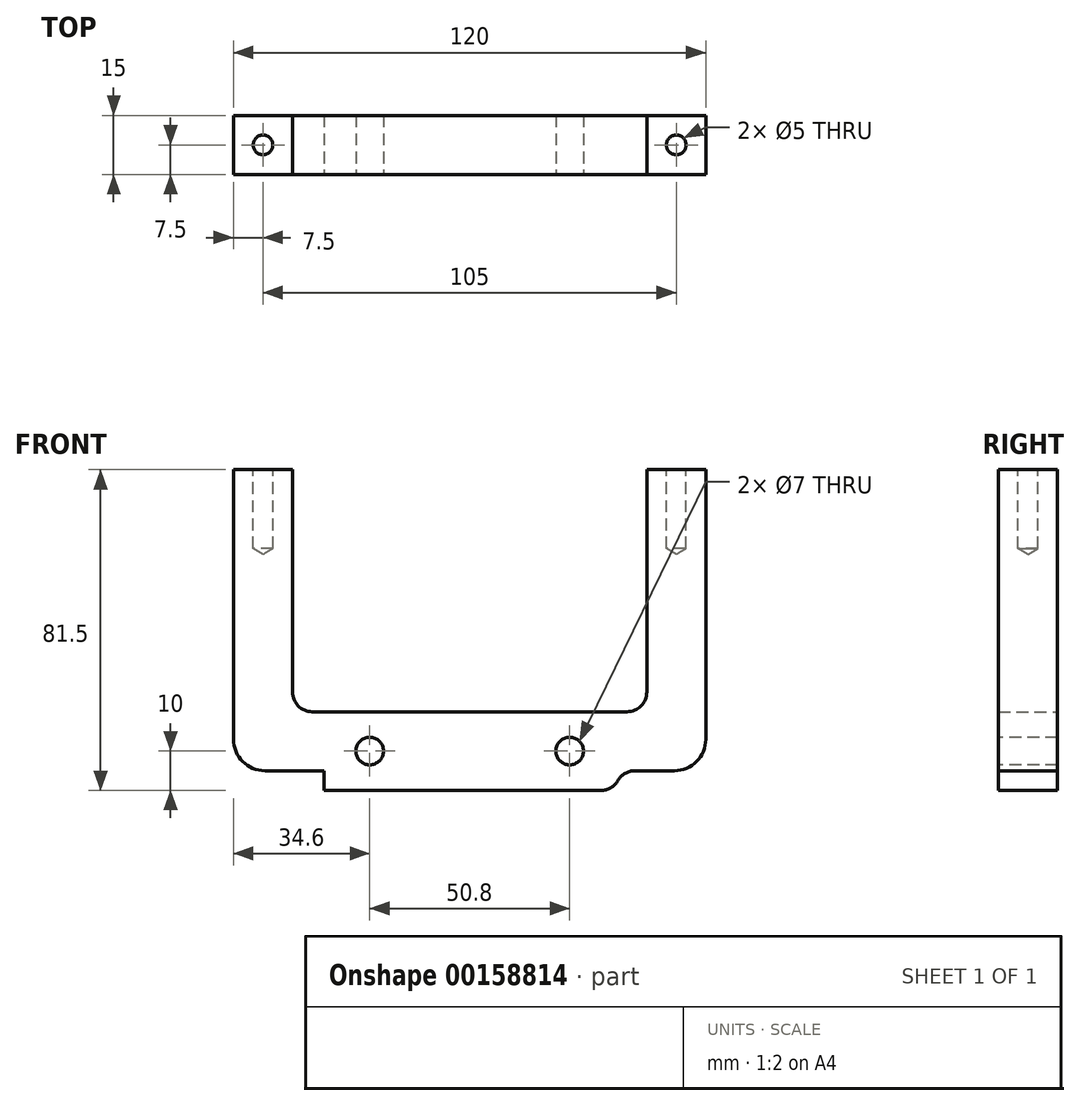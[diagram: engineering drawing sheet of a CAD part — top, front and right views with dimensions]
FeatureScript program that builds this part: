
annotation { "Feature Type Name" : "Feature", "Feature Type Description" : "" }
export const myFeature = defineFeature(function(context is Context, id is Id, definition is map)
    precondition{}
    {
        {
            var Q0;
            Q0=qCreatedBy(makeId("Front.planeOp"),FACE);
            var sketch = newSketch(context, id + "F0", { "sketchPlane" : qUnion([Q0])});
            skLineSegment(sketch, "E0", {"start": v(0, 0) * mm, "end": v(0, 61.5) * mm});
            skLineSegment(sketch, "E1", {"start": v(0, 0) * mm, "end": v(90, 0) * mm});
            skLineSegment(sketch, "E2", {"start": v(90, 0) * mm, "end": v(90, 61.5) * mm});
            skLineSegment(sketch, "E3.0", {"start": v(-15, -15) * mm, "end": v(-15, 61.5) * mm});
            skLineSegment(sketch, "E3.1", {"start": v(-15, -15) * mm, "end": v(105, -15) * mm});
            skLineSegment(sketch, "E3.2", {"start": v(105, -15) * mm, "end": v(105, 61.5) * mm});
            skLineSegment(sketch, "E4", {"start": v(-15, 61.5) * mm, "end": v(0, 61.5) * mm});
            skLineSegment(sketch, "E5", {"start": v(90, 61.5) * mm, "end": v(105, 61.5) * mm});
            skSolve(sketch);
        }
        {
            var Q0;
            Q0 = qSketchRegion(id + "F0", true);
            extrude(context, id + "F1", {"entities" : qUnion([Q0]), "depth" : 15 * mm});
        }
        {
            var Q0;
            Q0=makeQuery(id+"F1.opExtrude","CAP_FACE",FACE,{"disambiguationData":[OSD([sQuery(id+"F0.wireOp",EDGE,"E0"),sQuery(id+"F0.wireOp",EDGE,"E1"),sQuery(id+"F0.wireOp",EDGE,"E2"),sQuery(id+"F0.wireOp",EDGE,"E3.0"),sQuery(id+"F0.wireOp",EDGE,"E3.1"),sQuery(id+"F0.wireOp",EDGE,"E3.2"),sQuery(id+"F0.wireOp",EDGE,"E4"),sQuery(id+"F0.wireOp",EDGE,"E5")])],"isStart":false});
            var sketch = newSketch(context, id + "F2", { "sketchPlane" : qUnion([Q0])});
            skLineSegment(sketch, "E6.bottom", {"start": v(8, -15) * mm, "end": v(82, -15) * mm});
            skLineSegment(sketch, "E6.top", {"start": v(8, -20) * mm, "end": v(82, -20) * mm});
            skLineSegment(sketch, "E6.left", {"start": v(8, -15) * mm, "end": v(8, -20) * mm});
            skLineSegment(sketch, "E6.right", {"start": v(82, -15) * mm, "end": v(82, -20) * mm});
            skSolve(sketch);
        }
        {
            var Q0;
            Q0 = qSketchRegion(id + "F2", true);
            var Q1;
            Q1=makeQuery(id+"F1.opExtrude","CAP_FACE",FACE,{"disambiguationData":[OSD([sQuery(id+"F0.wireOp",EDGE,"E0"),sQuery(id+"F0.wireOp",EDGE,"E1"),sQuery(id+"F0.wireOp",EDGE,"E2"),sQuery(id+"F0.wireOp",EDGE,"E3.0"),sQuery(id+"F0.wireOp",EDGE,"E3.1"),sQuery(id+"F0.wireOp",EDGE,"E3.2"),sQuery(id+"F0.wireOp",EDGE,"E4"),sQuery(id+"F0.wireOp",EDGE,"E5")])],"isStart":true});
            extrude(context, id + "F3", {"entities" : qUnion([Q0]), "operationType" : NewBodyOperationType.ADD, "endBound" : BoundingType.UP_TO_SURFACE, "oppositeDirection" : true, "endBoundEntityFace" : qUnion([Q1]), "depth" : 25 * mm});
        }
        {
            var Q0;
            Q0=makeQuery(id+"F1.opExtrude","SWEPT_EDGE",EDGE,{"disambiguationData":[OSD([sQuery(id+"F0.wireOp",EDGE,"E0"),sQuery(id+"F0.wireOp",EDGE,"E1")])]});
            var Q1;
            Q1=makeQuery(id+"F1.opExtrude","SWEPT_EDGE",EDGE,{"disambiguationData":[OSD([sQuery(id+"F0.wireOp",EDGE,"E1"),sQuery(id+"F0.wireOp",EDGE,"E2")])]});
            var Q2;
            Q2=makeQuery(id+"F3.opExtrude","SWEPT_EDGE",EDGE,{"disambiguationData":[OSD([sQuery(id+"F0.wireOp",EDGE,"E3.1"),sQuery(id+"F2.wireOp",EDGE,"E6.bottom"),sQuery(id+"F2.wireOp",EDGE,"E6.left")])]});
            var Q3;
            Q3=makeQuery(id+"F3.opExtrude","SWEPT_EDGE",EDGE,{"disambiguationData":[OSD([sQuery(id+"F0.wireOp",EDGE,"E3.1"),sQuery(id+"F2.wireOp",EDGE,"E6.bottom"),sQuery(id+"F2.wireOp",EDGE,"E6.right")])]});
            fillet(context, id + "F4", {"entities" : qUnion([Q0, Q1, Q2, Q3]), "radius" : 5 * mm, "tangentPropagation" : true, "allowEdgeOverflow" : false});
        }
        {
            var Q0;
            Q0=makeQuery(id+"F1.opExtrude","SWEPT_EDGE",EDGE,{"disambiguationData":[OSD([sQuery(id+"F0.wireOp",EDGE,"E3.0"),sQuery(id+"F0.wireOp",EDGE,"E3.1")])]});
            var Q1;
            Q1=makeQuery(id+"F1.opExtrude","SWEPT_EDGE",EDGE,{"disambiguationData":[OSD([sQuery(id+"F0.wireOp",EDGE,"E3.1"),sQuery(id+"F0.wireOp",EDGE,"E3.2")])]});
            fillet(context, id + "F5", {"entities" : qUnion([Q0, Q1]), "radius" : 8 * mm, "tangentPropagation" : true, "allowEdgeOverflow" : false});
        }
        {
            var Q0;
            Q0=makeQuery(id+"F4.opFillet","BLEND_EDGE",EDGE,{"blendedFrom":[makeQuery(id+"F3.opExtrude","SWEPT_EDGE",EDGE,{"disambiguationData":[OSD([sQuery(id+"F0.wireOp",EDGE,"E3.1"),sQuery(id+"F2.wireOp",EDGE,"E6.bottom"),sQuery(id+"F2.wireOp",EDGE,"E6.right")])]}),makeQuery(id+"F3.opExtrude","SWEPT_FACE",FACE,{"disambiguationData":[OSD([sQuery(id+"F2.wireOp",EDGE,"E6.top")])]})],"blendedInto":[makeQuery(id+"F3.opExtrude","SWEPT_FACE",FACE,{"disambiguationData":[OSD([sQuery(id+"F2.wireOp",EDGE,"E6.top")])]})]});
            var Q1;
            Q1=makeQuery(id+"F4.opFillet","BLEND_EDGE",EDGE,{"blendedFrom":[makeQuery(id+"F3.opExtrude","SWEPT_EDGE",EDGE,{"disambiguationData":[OSD([sQuery(id+"F0.wireOp",EDGE,"E3.1"),sQuery(id+"F2.wireOp",EDGE,"E6.bottom"),sQuery(id+"F2.wireOp",EDGE,"E6.left")])]}),makeQuery(id+"F3.opExtrude","SWEPT_FACE",FACE,{"disambiguationData":[OSD([sQuery(id+"F2.wireOp",EDGE,"E6.top")])]})],"blendedInto":[makeQuery(id+"F3.opExtrude","SWEPT_FACE",FACE,{"disambiguationData":[OSD([sQuery(id+"F2.wireOp",EDGE,"E6.top")])]})]});
            fillet(context, id + "F6", {"entities" : qUnion([Q0, Q1]), "radius" : 5 * mm, "tangentPropagation" : true, "allowEdgeOverflow" : false});
        }
        {
            var Q0;
            Q0=makeQuery(id+"F3.boolean.opBoolean","MERGE",FACE,{"derivedFrom":[makeQuery(id+"F1.opExtrude","CAP_FACE",FACE,{"disambiguationData":[OSD([sQuery(id+"F0.wireOp",EDGE,"E0"),sQuery(id+"F0.wireOp",EDGE,"E1"),sQuery(id+"F0.wireOp",EDGE,"E2"),sQuery(id+"F0.wireOp",EDGE,"E3.0"),sQuery(id+"F0.wireOp",EDGE,"E3.1"),sQuery(id+"F0.wireOp",EDGE,"E3.2"),sQuery(id+"F0.wireOp",EDGE,"E4"),sQuery(id+"F0.wireOp",EDGE,"E5")])],"isStart":false}),makeQuery(id+"F3.opExtrude","CAP_FACE",FACE,{"disambiguationData":[OSD([sQuery(id+"F2.wireOp",EDGE,"E6.bottom"),sQuery(id+"F2.wireOp",EDGE,"E6.top"),sQuery(id+"F2.wireOp",EDGE,"E6.left"),sQuery(id+"F2.wireOp",EDGE,"E6.right")])],"isStart":true})]});
            var sketch = newSketch(context, id + "F7", { "sketchPlane" : qUnion([Q0])});
            skCircle(sketch, "E7", {"center": v(19.6, -10) * mm, "radius": 3.5 * mm});
            skCircle(sketch, "E8", {"center": v(70.4, -10) * mm, "radius": 3.5 * mm});
            skLineSegment(sketch, "E9", {"start": v(19.6, -10) * mm, "end": v(70.4, -10) * mm, "construction": true});
            skLineSegment(sketch, "E10", {"start": v(45, -10) * mm, "end": v(45, 0) * mm, "construction": true});
            skSolve(sketch);
        }
        {
            var Q0;
            Q0=sQuery(id+"F7.wireOp",VERTEX,"E7.center");
            var Q1;
            Q1=sQuery(id+"F7.wireOp",VERTEX,"E9.end");
            var Q2;
            Q2=makeQuery(id+"F1.opExtrude","SWEPT_BODY",BODY,{"disambiguationData":[OSD([sQuery(id+"F0.wireOp",EDGE,"E0"),sQuery(id+"F0.wireOp",EDGE,"E1"),sQuery(id+"F0.wireOp",EDGE,"E2"),sQuery(id+"F0.wireOp",EDGE,"E3.0"),sQuery(id+"F0.wireOp",EDGE,"E3.1"),sQuery(id+"F0.wireOp",EDGE,"E3.2"),sQuery(id+"F0.wireOp",EDGE,"E4"),sQuery(id+"F0.wireOp",EDGE,"E5")])]});
            hole(context, id + "F8", {"style" : HoleStyle.SIMPLE, "endStyle" : HoleEndStyle.THROUGH, "holeDiameter" : 7 * mm, "locations" : qUnion([Q0, Q1]), "scope" : qUnion([Q2]), "isTappedThrough" : true});
        }
        {
            var Q0;
            Q0=makeQuery(id+"F1.opExtrude","SWEPT_FACE",FACE,{"disambiguationData":[OSD([sQuery(id+"F0.wireOp",EDGE,"E4")])]});
            var sketch = newSketch(context, id + "F9", { "sketchPlane" : qUnion([Q0])});
            skLineSegment(sketch, "E11", {"start": v(-15, -7.5) * mm, "end": v(0, -7.5) * mm, "construction": true});
            skLineSegment(sketch, "E12", {"start": v(0, -7.5) * mm, "end": v(-7.5, -15) * mm, "construction": true});
            skLineSegment(sketch, "E13", {"start": v(-7.5, -15) * mm, "end": v(-7.5, -7.5) * mm, "construction": true});
            skSolve(sketch);
        }
        {
            var Q0;
            Q0=makeQuery(id+"F1.opExtrude","SWEPT_FACE",FACE,{"disambiguationData":[OSD([sQuery(id+"F0.wireOp",EDGE,"E5")])]});
            var sketch = newSketch(context, id + "F10", { "sketchPlane" : qUnion([Q0])});
            skLineSegment(sketch, "E14", {"start": v(105, -7.5) * mm, "end": v(90, -7.5) * mm, "construction": true});
            skLineSegment(sketch, "E15", {"start": v(97.5, 0) * mm, "end": v(97.5, -7.5) * mm, "construction": true});
            skSolve(sketch);
        }
        {
            var Q0;
            Q0=sQuery(id+"F9.wireOp",VERTEX,"E13.end");
            var Q1;
            Q1=sQuery(id+"F10.wireOp",VERTEX,"E15.end");
            var Q2;
            Q2=makeQuery(id+"F1.opExtrude","SWEPT_BODY",BODY,{"disambiguationData":[OSD([sQuery(id+"F0.wireOp",EDGE,"E0"),sQuery(id+"F0.wireOp",EDGE,"E1"),sQuery(id+"F0.wireOp",EDGE,"E2"),sQuery(id+"F0.wireOp",EDGE,"E3.0"),sQuery(id+"F0.wireOp",EDGE,"E3.1"),sQuery(id+"F0.wireOp",EDGE,"E3.2"),sQuery(id+"F0.wireOp",EDGE,"E4"),sQuery(id+"F0.wireOp",EDGE,"E5")])]});
            hole(context, id + "F11", {"style" : HoleStyle.SIMPLE, "endStyle" : HoleEndStyle.BLIND, "holeDiameter" : 5 * mm, "holeDepth" : 20 * mm, "locations" : qUnion([Q0, Q1]), "scope" : qUnion([Q2])});
        }
    });
